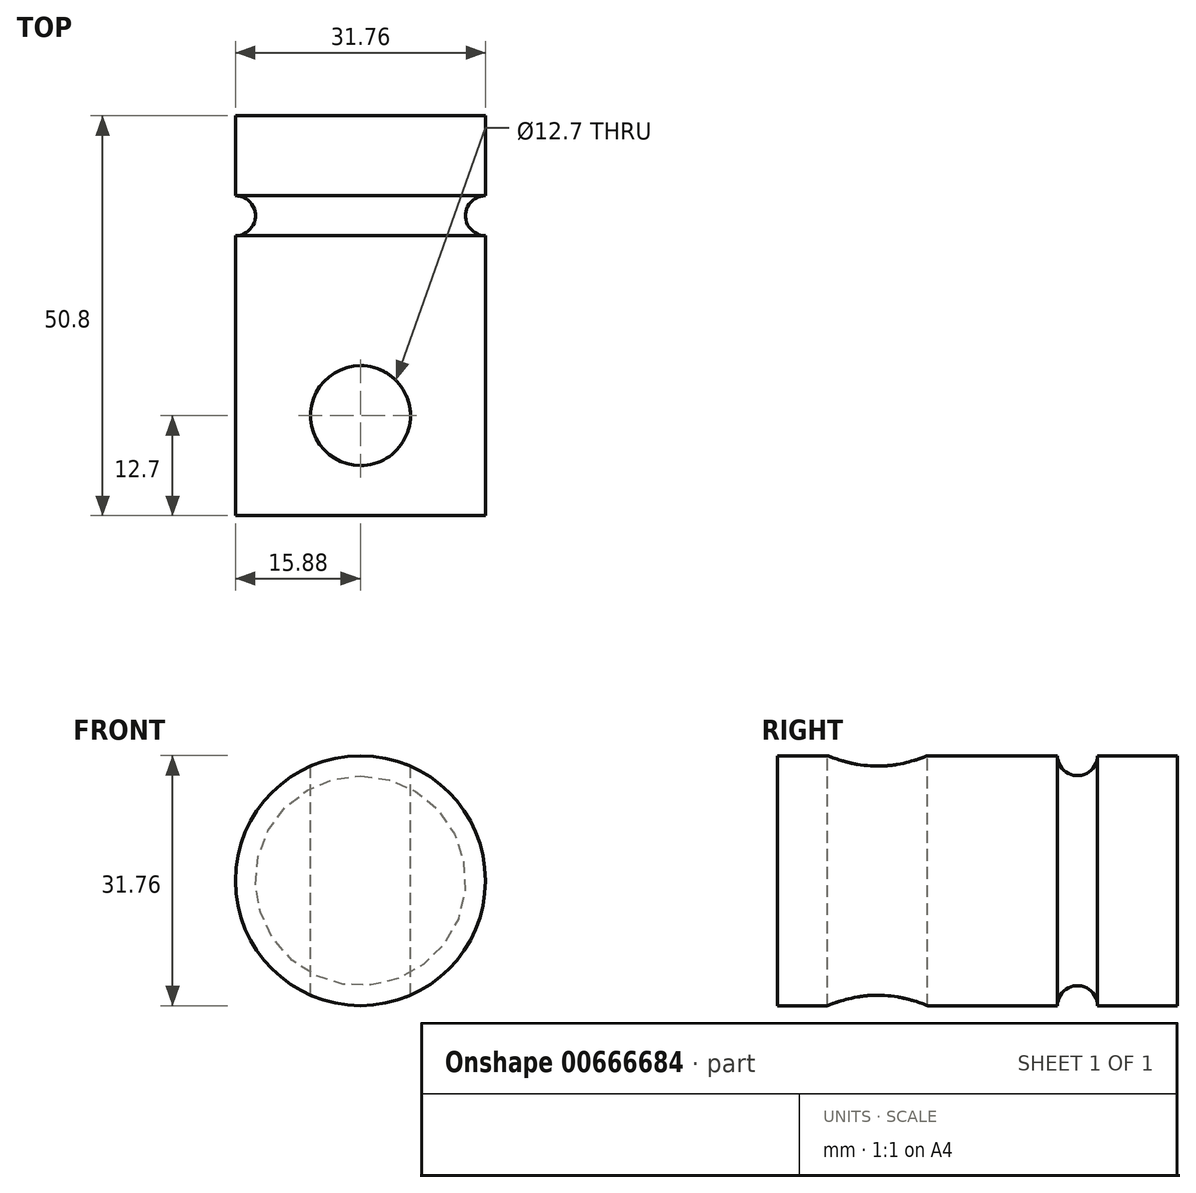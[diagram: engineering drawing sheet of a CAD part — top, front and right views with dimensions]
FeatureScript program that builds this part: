
annotation { "Feature Type Name" : "Feature", "Feature Type Description" : "" }
export const myFeature = defineFeature(function(context is Context, id is Id, definition is map)
    precondition{}
    {
        {
            var Q0;
            Q0=qCreatedBy(makeId("Front.planeOp"),FACE);
            var sketch = newSketch(context, id + "F0", { "sketchPlane" : qUnion([Q0])});
            skCircle(sketch, "E0", {"center": v(0, 0) * mm, "radius": 15.87 * mm});
            skSolve(sketch);
        }
        {
            var Q0;
            Q0 = qSketchRegion(id + "F0", false);
            extrude(context, id + "F1", {"entities" : qUnion([Q0]), "depth" : 50.8 * mm});
        }
        {
            var Q0;
            Q0=makeQuery(id+"F1.opExtrude","CAP_FACE",FACE,{"disambiguationData":[OSD([sQuery(id+"F0.wireOp",EDGE,"E0")])],"isStart":true});
            cPlane(context, id + "F2", {"entities" : qUnion([Q0]), "cplaneType" : CPlaneType.OFFSET, "offset" : 12.7 * mm, "oppositeDirection" : true, "width" : 152.4 * mm, "height" : 152.4 * mm});
        }
        {
            var Q0;
            Q0=qCreatedBy(id+"F2.planeOp",FACE);
            var sketch = newSketch(context, id + "F3", { "sketchPlane" : qUnion([Q0])});
            skCircle(sketch, "E0", {"center": v(0, 0) * mm, "radius": 15.87 * mm});
            skSolve(sketch);
        }
        {
            var Q0;
            Q0=qCreatedBy(makeId("Right.planeOp"),FACE);
            var sketch = newSketch(context, id + "F4", { "sketchPlane" : qUnion([Q0])});
            skCircle(sketch, "E1", {"center": v(-12.7, 15.87) * mm, "radius": 2.54 * mm});
            skSolve(sketch);
        }
        {
            var Q0;
            Q0=makeQuery(id+"F4.imprint","IMPRINT",FACE,{"disambiguationData":[TD([[makeQuery(id+"F4.imprint","IMPRINT",EDGE,{"derivedFrom":sQuery(id+"F4.wireOp",EDGE,"E1")}),1.0]])]});
            var Q1;
            Q1=sQuery(id+"F3.wireOp",EDGE,"E0");
            sweep(context, id + "F5", {"operationType" : NewBodyOperationType.REMOVE, "profiles" : qUnion([Q0]), "path" : qUnion([Q1])});
        }
        {
            var Q0;
            Q0=qCreatedBy(makeId("Top.planeOp"),FACE);
            var sketch = newSketch(context, id + "F6", { "sketchPlane" : qUnion([Q0])});
            skCircle(sketch, "E2", {"center": v(0, -38.1) * mm, "radius": 6.35 * mm});
            skSolve(sketch);
        }
        {
            var Q0;
            Q0 = qSketchRegion(id + "F6", false);
            extrude(context, id + "F7", {"entities" : qUnion([Q0]), "operationType" : NewBodyOperationType.REMOVE, "endBound" : BoundingType.UP_TO_NEXT, "oppositeDirection" : true, "hasSecondDirection" : true, "secondDirectionBound" : SecondDirectionBoundingType.UP_TO_NEXT, "secondDirectionOppositeDirection" : false});
        }
    });
